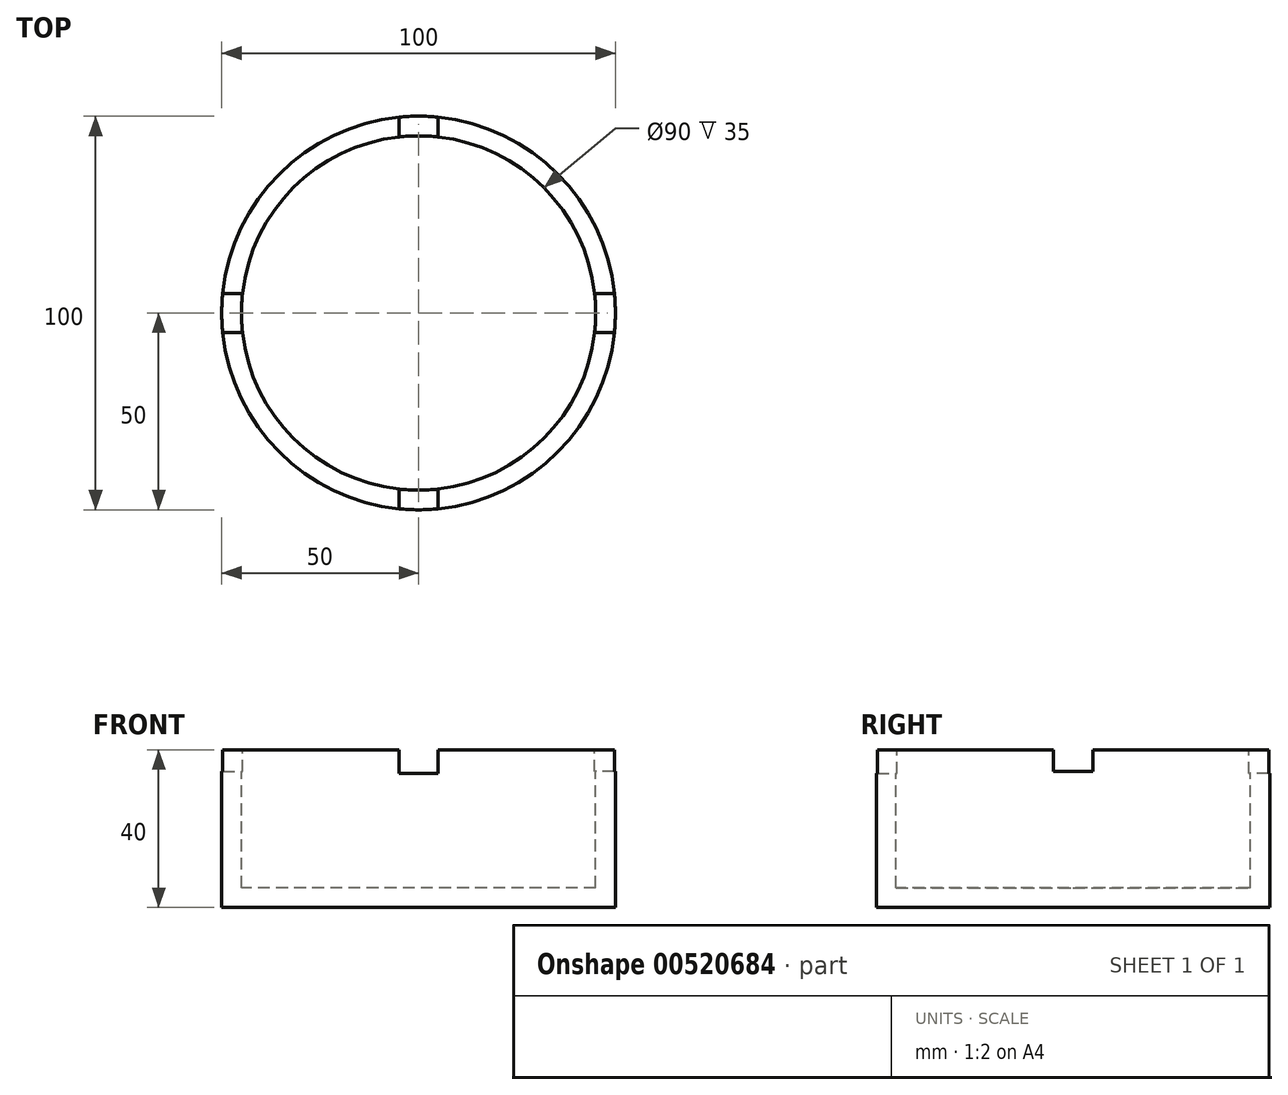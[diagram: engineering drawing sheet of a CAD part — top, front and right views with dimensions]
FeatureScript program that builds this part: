
annotation { "Feature Type Name" : "Feature", "Feature Type Description" : "" }
export const myFeature = defineFeature(function(context is Context, id is Id, definition is map)
    precondition{}
    {
        {
            var Q0;
            Q0=qCreatedBy(makeId("Top.planeOp"),FACE);
            var sketch = newSketch(context, id + "F0", { "sketchPlane" : qUnion([Q0])});
            skCircle(sketch, "E0", {"center": v(0, 0) * mm, "radius": 50 * mm});
            skSolve(sketch);
        }
        {
            var Q0;
            Q0=qSketchRegion(id+"F0",true);
            extrude(context, id + "F1", {"entities" : qUnion([Q0]), "depth" : 40 * mm, "offsetDistance" : 25 * mm});
        }
        {
            var Q0;
            Q0=makeQuery(id+"F1.opExtrude","CAP_FACE",FACE,{"disambiguationData":[OSD([sQuery(id+"F0.wireOp",EDGE,"E0")])],"isStart":false});
            var sketch = newSketch(context, id + "F2", { "sketchPlane" : qUnion([Q0])});
            skCircle(sketch, "E1", {"center": v(0, 0) * mm, "radius": 45 * mm});
            skSolve(sketch);
        }
        {
            var Q0;
            Q0=qSketchRegion(id+"F2",true);
            extrude(context, id + "F3", {"entities" : qUnion([Q0]), "operationType" : NewBodyOperationType.REMOVE, "oppositeDirection" : true, "depth" : 35 * mm, "offsetDistance" : 25 * mm});
        }
        {
            var Q0;
            Q0=qCreatedBy(makeId("Front.planeOp"),FACE);
            var sketch = newSketch(context, id + "F4", { "sketchPlane" : qUnion([Q0])});
            skLineSegment(sketch, "E2.bottom", {"start": v(5, 40) * mm, "end": v(-5, 40) * mm});
            skLineSegment(sketch, "E2.top", {"start": v(5, 34) * mm, "end": v(-5, 34) * mm});
            skLineSegment(sketch, "E2.left", {"start": v(5, 40) * mm, "end": v(5, 34) * mm});
            skLineSegment(sketch, "E2.right", {"start": v(-5, 40) * mm, "end": v(-5, 34) * mm});
            skSolve(sketch);
        }
        {
            var Q0;
            Q0=qSketchRegion(id+"F4",true);
            extrude(context, id + "F5", {"entities" : qUnion([Q0]), "operationType" : NewBodyOperationType.REMOVE, "oppositeDirection" : true, "depth" : 50 * mm, "offsetDistance" : 25 * mm});
        }
        {
            var Q0;
            Q0=qCreatedBy(makeId("Front.planeOp"),FACE);
            var sketch = newSketch(context, id + "F6", { "sketchPlane" : qUnion([Q0])});
            skLineSegment(sketch, "E3.bottom", {"start": v(5, 40) * mm, "end": v(-5, 40) * mm});
            skLineSegment(sketch, "E3.top", {"start": v(5, 34) * mm, "end": v(-5, 34) * mm});
            skLineSegment(sketch, "E3.left", {"start": v(5, 40) * mm, "end": v(5, 34) * mm});
            skLineSegment(sketch, "E3.right", {"start": v(-5, 40) * mm, "end": v(-5, 34) * mm});
            skSolve(sketch);
        }
        {
            var Q0;
            Q0=qSketchRegion(id+"F6",true);
            extrude(context, id + "F7", {"entities" : qUnion([Q0]), "operationType" : NewBodyOperationType.REMOVE, "depth" : 50 * mm, "offsetDistance" : 25 * mm});
        }
        {
            var Q0;
            Q0=qCreatedBy(makeId("Right.planeOp"),FACE);
            var sketch = newSketch(context, id + "F8", { "sketchPlane" : qUnion([Q0])});
            skLineSegment(sketch, "E4.bottom", {"start": v(5, 40) * mm, "end": v(-5, 40) * mm});
            skLineSegment(sketch, "E4.top", {"start": v(5, 34.5) * mm, "end": v(-5, 34.5) * mm});
            skLineSegment(sketch, "E4.left", {"start": v(5, 40) * mm, "end": v(5, 34.5) * mm});
            skLineSegment(sketch, "E4.right", {"start": v(-5, 40) * mm, "end": v(-5, 34.5) * mm});
            skSolve(sketch);
        }
        {
            var Q0;
            Q0=qSketchRegion(id+"F8",true);
            extrude(context, id + "F9", {"entities" : qUnion([Q0]), "operationType" : NewBodyOperationType.REMOVE, "oppositeDirection" : true, "depth" : 50 * mm, "offsetDistance" : 25 * mm});
        }
        {
            var Q0;
            Q0=qCreatedBy(makeId("Right.planeOp"),FACE);
            var sketch = newSketch(context, id + "F10", { "sketchPlane" : qUnion([Q0])});
            skLineSegment(sketch, "E5.bottom", {"start": v(5, 40) * mm, "end": v(-5, 40) * mm});
            skLineSegment(sketch, "E5.top", {"start": v(5, 34.5) * mm, "end": v(-5, 34.5) * mm});
            skLineSegment(sketch, "E5.left", {"start": v(5, 40) * mm, "end": v(5, 34.5) * mm});
            skLineSegment(sketch, "E5.right", {"start": v(-5, 40) * mm, "end": v(-5, 34.5) * mm});
            skSolve(sketch);
        }
        {
            var Q0;
            Q0=qSketchRegion(id+"F10",true);
            extrude(context, id + "F11", {"entities" : qUnion([Q0]), "operationType" : NewBodyOperationType.REMOVE, "depth" : 50 * mm, "offsetDistance" : 25 * mm});
        }
    });
